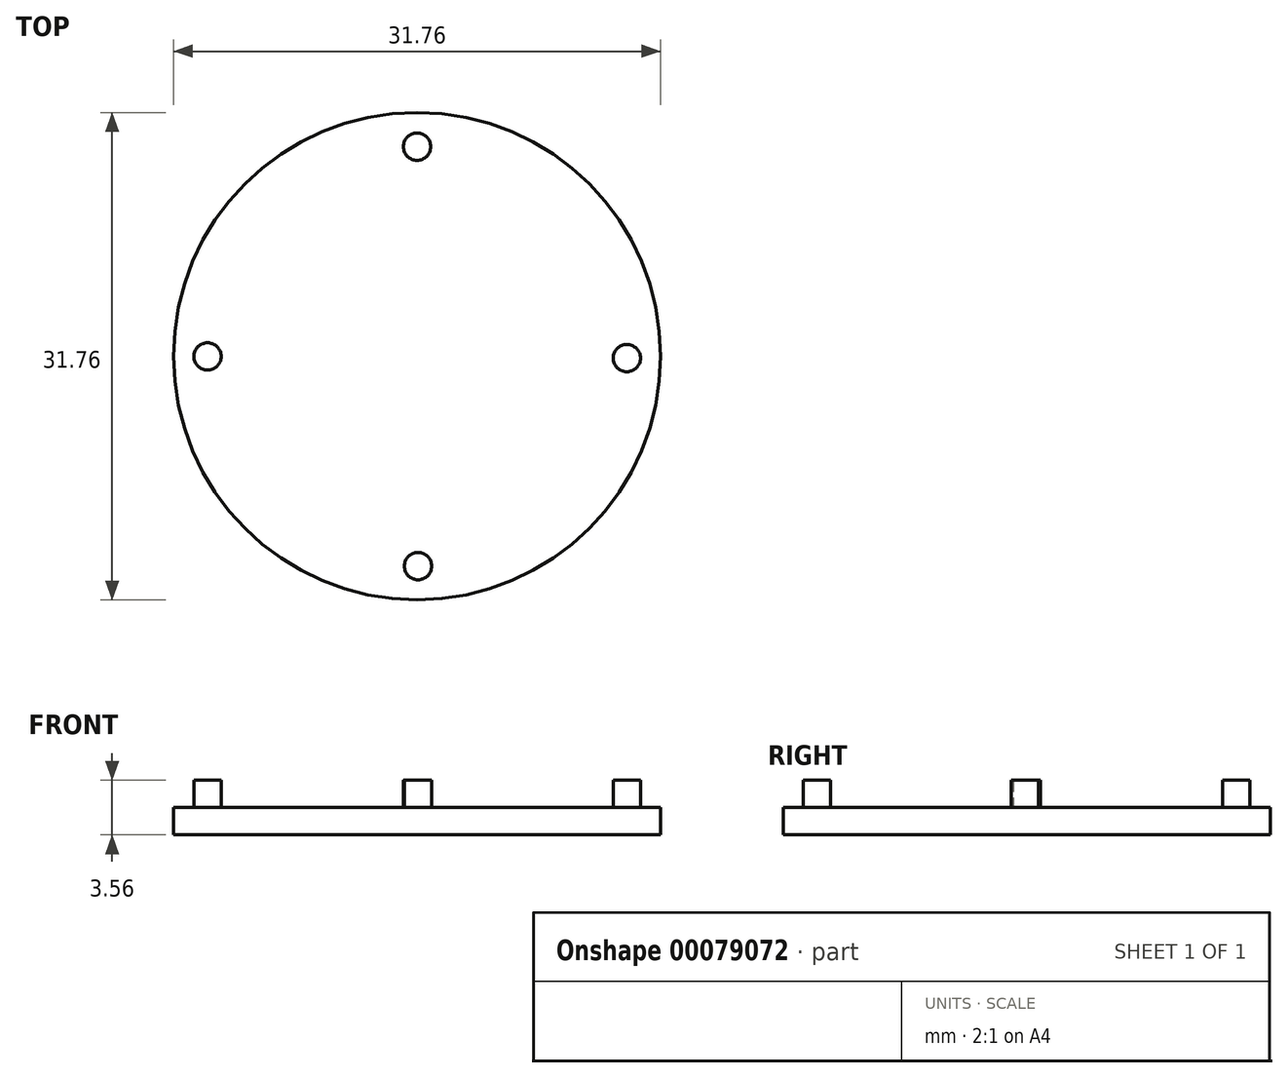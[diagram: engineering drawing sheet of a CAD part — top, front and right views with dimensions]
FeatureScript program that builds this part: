
annotation { "Feature Type Name" : "Feature", "Feature Type Description" : "" }
export const myFeature = defineFeature(function(context is Context, id is Id, definition is map)
    precondition{}
    {
        {
            var Q0;
            Q0=qCreatedBy(makeId("Top.planeOp"),FACE);
            var sketch = newSketch(context, id + "F0", { "sketchPlane" : qUnion([Q0])});
            skCircle(sketch, "E0", {"center": v(0, 0) * mm, "radius": 15.88 * mm});
            skSolve(sketch);
        }
        {
            var Q0;
            Q0=qSketchRegion(id+"F0",true);
            extrude(context, id + "F1", {"entities" : qUnion([Q0]), "oppositeDirection" : true, "depth" : 1.78 * mm});
        }
        {
            var Q0;
            Q0=makeQuery(id+"F1.opExtrude","CAP_FACE",FACE,{"disambiguationData":[OSD([sQuery(id+"F0.wireOp",EDGE,"E0")])],"isStart":true});
            var sketch = newSketch(context, id + "F2", { "sketchPlane" : qUnion([Q0])});
            skCircle(sketch, "E1", {"center": v(0, 0) * mm, "radius": 12.7 * mm});
            skSolve(sketch);
        }
        {
            var Q0;
            Q0=makeQuery(id+"F2.imprint","IMPRINT",FACE,{"disambiguationData":[TD([[makeQuery(id+"F2.imprint","IMPRINT",EDGE,{"derivedFrom":sQuery(id+"F2.wireOp",EDGE,"E1")}),-1.0]])]});
            var sketch = newSketch(context, id + "F3", { "sketchPlane" : qUnion([Q0])});
            skCircle(sketch, "E2", {"center": v(0, 13.65) * mm, "radius": 0.89 * mm});
            skCircle(sketch, "E3", {"center": v(-13.66, -0.02) * mm, "radius": 0.89 * mm});
            skCircle(sketch, "E4", {"center": v(0.06, -13.68) * mm, "radius": 0.89 * mm});
            skCircle(sketch, "E5", {"center": v(13.67, -0.12) * mm, "radius": 0.89 * mm});
            skSolve(sketch);
        }
        {
            var Q0;
            Q0=qSketchRegion(id+"F3",true);
            extrude(context, id + "F4", {"entities" : qUnion([Q0]), "operationType" : NewBodyOperationType.ADD, "depth" : 1.78 * mm});
        }
    });
